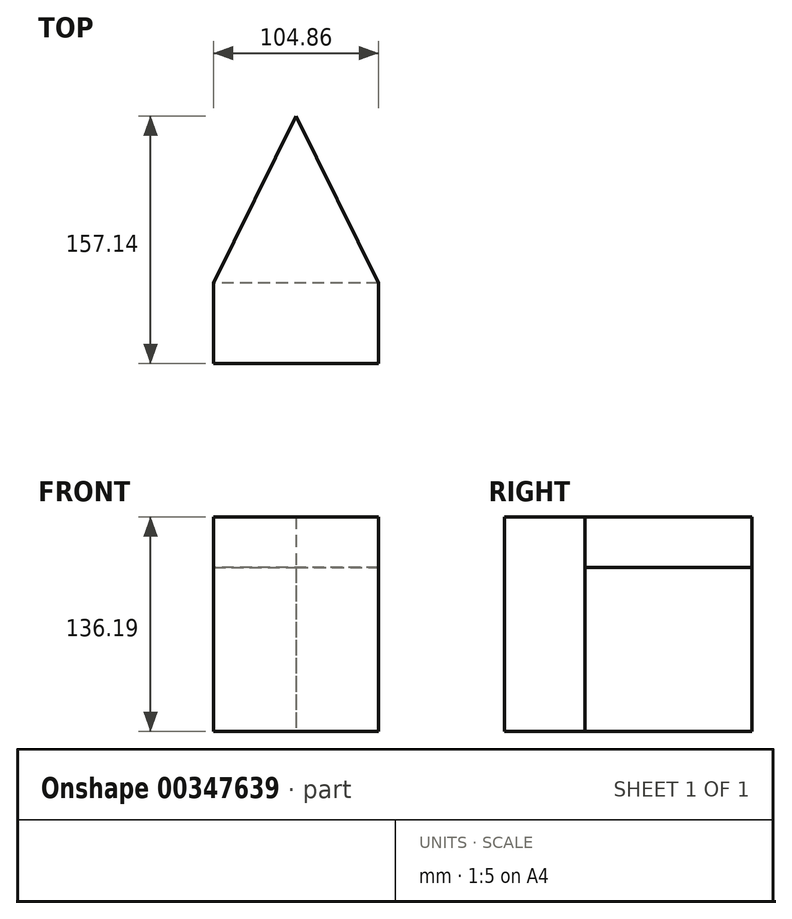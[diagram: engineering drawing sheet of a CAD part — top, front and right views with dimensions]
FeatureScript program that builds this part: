
annotation { "Feature Type Name" : "Feature", "Feature Type Description" : "" }
export const myFeature = defineFeature(function(context is Context, id is Id, definition is map)
    precondition{}
    {
        {
            var Q0;
            Q0=qCreatedBy(makeId("Top.planeOp"),FACE);
            var sketch = newSketch(context, id + "F0", { "sketchPlane" : qUnion([Q0])});
            skLineSegment(sketch, "E0.bottom", {"start": v(52.43, 25.56) * mm, "end": v(-52.43, 25.56) * mm});
            skLineSegment(sketch, "E0.top", {"start": v(52.43, -25.56) * mm, "end": v(-52.43, -25.56) * mm});
            skLineSegment(sketch, "E0.left", {"start": v(52.43, 25.56) * mm, "end": v(52.43, -25.56) * mm});
            skLineSegment(sketch, "E0.right", {"start": v(-52.43, 25.56) * mm, "end": v(-52.43, -25.56) * mm});
            skPoint(sketch, "E0.middle", {"position": v(0, 0) * mm});
            skLineSegment(sketch, "E1", {"start": v(0, 0) * mm, "end": v(0, 131.58) * mm});
            skLineSegment(sketch, "E2", {"start": v(0, 131.58) * mm, "end": v(52.43, 25.56) * mm});
            skLineSegment(sketch, "E3", {"start": v(-52.43, 25.56) * mm, "end": v(0, 131.58) * mm});
            skSolve(sketch);
        }
        {
            var Q0;
            {var subQ0=sQuery(id+"F0.wireOp",EDGE,"E2");Q0=makeQuery(id+"F0.imprint","IMPRINT",FACE,{"disambiguationData":[TD([[makeQuery(id+"F0.imprint","IMPRINT",EDGE,{"derivedFrom":subQ0}),-1.0]])]});}
            var Q1;
            {var subQ0=sQuery(id+"F0.wireOp",EDGE,"E3");Q1=makeQuery(id+"F0.imprint","IMPRINT",FACE,{"disambiguationData":[TD([[makeQuery(id+"F0.imprint","IMPRINT",EDGE,{"derivedFrom":subQ0}),-1.0]])]});}
            extrude(context, id + "F1", {"entities" : qUnion([Q0, Q1]), "depth" : 104.1 * mm});
        }
        {
            var Q0;
            Q0 = qSketchRegion(id + "F0", true);
            var Q1;
            {var subQ0=sQuery(id+"F0.wireOp",EDGE,"E2");Q1=makeQuery(id+"F0.imprint","IMPRINT",FACE,{"disambiguationData":[TD([[makeQuery(id+"F0.imprint","IMPRINT",EDGE,{"derivedFrom":subQ0}),-1.0]])]});}
            extrude(context, id + "F2", {"entities" : qUnion([Q0, Q1]), "depth" : 136.2 * mm});
        }
    });
